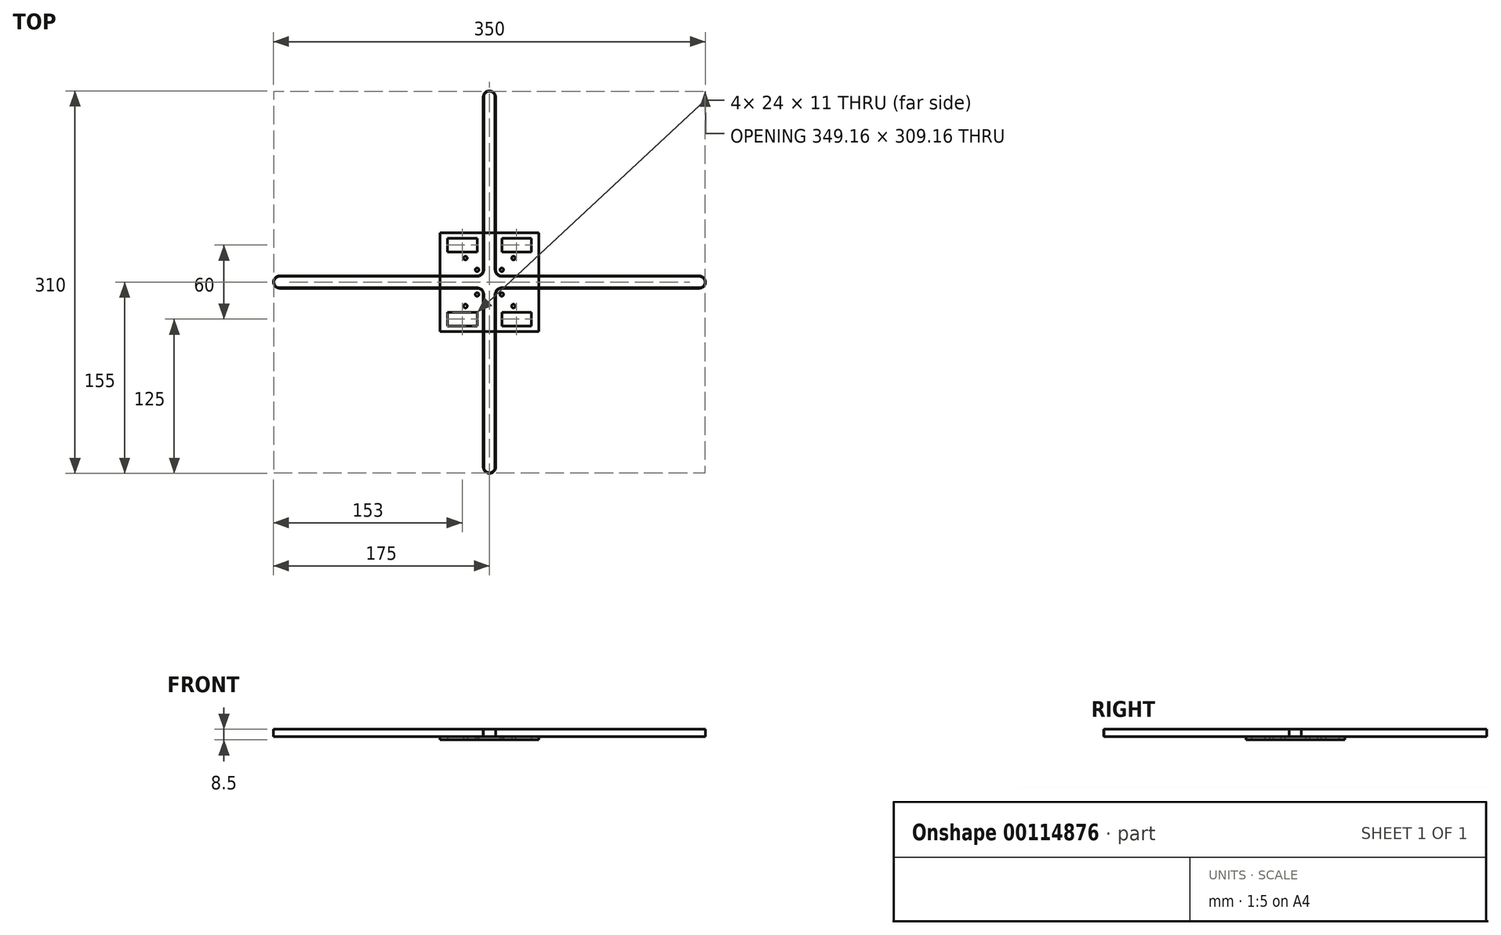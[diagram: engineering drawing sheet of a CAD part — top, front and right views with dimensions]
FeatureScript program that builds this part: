
annotation { "Feature Type Name" : "Feature", "Feature Type Description" : "" }
export const myFeature = defineFeature(function(context is Context, id is Id, definition is map)
    precondition{}
    {
        {
            var Q0;
            Q0=qCreatedBy(makeId("Top.planeOp"),FACE);
            var sketch = newSketch(context, id + "F0", { "sketchPlane" : qUnion([Q0])});
            skLineSegment(sketch, "E0", {"start": v(-126.92, 30) * mm, "end": v(134.24, 30) * mm, "construction": true});
            skLineSegment(sketch, "E1", {"start": v(-126.68, -30) * mm, "end": v(132.4, -30) * mm, "construction": true});
            skLineSegment(sketch, "E2", {"start": v(-22, 80.91) * mm, "end": v(-22, -74.2) * mm, "construction": true});
            skLineSegment(sketch, "E3", {"start": v(22, 83.6) * mm, "end": v(22, -72.05) * mm, "construction": true});
            skLineSegment(sketch, "E4.bottom", {"start": v(-40, 40) * mm, "end": v(40, 40) * mm});
            skLineSegment(sketch, "E4.top", {"start": v(-40, -40) * mm, "end": v(40, -40) * mm});
            skLineSegment(sketch, "E4.left", {"start": v(-40, 40) * mm, "end": v(-40, -40) * mm});
            skLineSegment(sketch, "E4.right", {"start": v(40, 40) * mm, "end": v(40, -40) * mm});
            skPoint(sketch, "E4.middle", {"position": v(0, 0) * mm});
            skLineSegment(sketch, "E5.bottom", {"start": v(-34, 35.5) * mm, "end": v(-10, 35.5) * mm});
            skLineSegment(sketch, "E5.top", {"start": v(-34, 24.5) * mm, "end": v(-10, 24.5) * mm});
            skLineSegment(sketch, "E5.left", {"start": v(-34, 35.5) * mm, "end": v(-34, 24.5) * mm});
            skLineSegment(sketch, "E5.right", {"start": v(-10, 35.5) * mm, "end": v(-10, 24.5) * mm});
            skPoint(sketch, "E5.middle", {"position": v(-22, 30) * mm});
            skLineSegment(sketch, "E6.bottom", {"start": v(10, 35.5) * mm, "end": v(34, 35.5) * mm});
            skLineSegment(sketch, "E6.top", {"start": v(10, 24.5) * mm, "end": v(34, 24.5) * mm});
            skLineSegment(sketch, "E6.left", {"start": v(10, 35.5) * mm, "end": v(10, 24.5) * mm});
            skLineSegment(sketch, "E6.right", {"start": v(34, 35.5) * mm, "end": v(34, 24.5) * mm});
            skPoint(sketch, "E6.middle", {"position": v(22, 30) * mm});
            skLineSegment(sketch, "E7.bottom", {"start": v(-34, -24.5) * mm, "end": v(-10, -24.5) * mm});
            skLineSegment(sketch, "E7.top", {"start": v(-34, -35.5) * mm, "end": v(-10, -35.5) * mm});
            skLineSegment(sketch, "E7.left", {"start": v(-34, -24.5) * mm, "end": v(-34, -35.5) * mm});
            skLineSegment(sketch, "E7.right", {"start": v(-10, -24.5) * mm, "end": v(-10, -35.5) * mm});
            skPoint(sketch, "E7.middle", {"position": v(-22, -30) * mm});
            skLineSegment(sketch, "E8.bottom", {"start": v(10, -24.5) * mm, "end": v(34, -24.5) * mm});
            skLineSegment(sketch, "E8.top", {"start": v(10, -35.5) * mm, "end": v(34, -35.5) * mm});
            skLineSegment(sketch, "E8.left", {"start": v(10, -24.5) * mm, "end": v(10, -35.5) * mm});
            skLineSegment(sketch, "E8.right", {"start": v(34, -24.5) * mm, "end": v(34, -35.5) * mm});
            skPoint(sketch, "E8.middle", {"position": v(22, -30) * mm});
            skLineSegment(sketch, "E9.bottom", {"start": v(-10, 10) * mm, "end": v(10, 10) * mm, "construction": true});
            skLineSegment(sketch, "E9.top", {"start": v(-10, -10) * mm, "end": v(10, -10) * mm, "construction": true});
            skLineSegment(sketch, "E9.left", {"start": v(-10, 10) * mm, "end": v(-10, -10) * mm, "construction": true});
            skLineSegment(sketch, "E9.right", {"start": v(10, 10) * mm, "end": v(10, -10) * mm, "construction": true});
            skCircle(sketch, "E10", {"center": v(-10, 10) * mm, "radius": 1.5 * mm});
            skCircle(sketch, "E11", {"center": v(10, 10) * mm, "radius": 1.5 * mm});
            skCircle(sketch, "E12", {"center": v(-10, -10) * mm, "radius": 1.5 * mm});
            skCircle(sketch, "E13", {"center": v(10, -10) * mm, "radius": 1.5 * mm});
            skCircle(sketch, "E14", {"center": v(-10, 10) * mm, "radius": 5.75 * mm, "construction": true});
            skLineSegment(sketch, "E15", {"start": v(40, 40) * mm, "end": v(-40, -40) * mm, "construction": true});
            skLineSegment(sketch, "E16", {"start": v(-40, 40) * mm, "end": v(40, -40) * mm, "construction": true});
            skCircle(sketch, "E17", {"center": v(0, 0) * mm, "radius": 27.5 * mm, "construction": true});
            skCircle(sketch, "E18", {"center": v(19.44, 19.44) * mm, "radius": 1.5 * mm});
            skCircle(sketch, "E19", {"center": v(-19.44, 19.44) * mm, "radius": 1.5 * mm});
            skCircle(sketch, "E20", {"center": v(-19.44, -19.44) * mm, "radius": 1.5 * mm});
            skCircle(sketch, "E21", {"center": v(19.44, -19.44) * mm, "radius": 1.5 * mm});
            skSolve(sketch);
        }
        {
            var Q0;
            Q0 = qSketchRegion(id + "F0", true);
            extrude(context, id + "F1", {"entities" : qUnion([Q0]), "depth" : 2.5 * mm});
        }
        {
            var Q0;
            Q0=makeQuery(id+"F1.opExtrude","CAP_FACE",FACE,{"disambiguationData":[OSD([sQuery(id+"F0.wireOp",EDGE,"E4.bottom"),sQuery(id+"F0.wireOp",EDGE,"E4.top"),sQuery(id+"F0.wireOp",EDGE,"E4.left"),sQuery(id+"F0.wireOp",EDGE,"E4.right"),sQuery(id+"F0.wireOp",EDGE,"E5.bottom"),sQuery(id+"F0.wireOp",EDGE,"E5.top"),sQuery(id+"F0.wireOp",EDGE,"E5.left"),sQuery(id+"F0.wireOp",EDGE,"E5.right"),sQuery(id+"F0.wireOp",EDGE,"E6.bottom"),sQuery(id+"F0.wireOp",EDGE,"E6.top"),sQuery(id+"F0.wireOp",EDGE,"E6.left"),sQuery(id+"F0.wireOp",EDGE,"E6.right"),sQuery(id+"F0.wireOp",EDGE,"E7.bottom"),sQuery(id+"F0.wireOp",EDGE,"E7.top"),sQuery(id+"F0.wireOp",EDGE,"E7.left"),sQuery(id+"F0.wireOp",EDGE,"E7.right"),sQuery(id+"F0.wireOp",EDGE,"E8.bottom"),sQuery(id+"F0.wireOp",EDGE,"E8.top"),sQuery(id+"F0.wireOp",EDGE,"E8.left"),sQuery(id+"F0.wireOp",EDGE,"E8.right"),sQuery(id+"F0.wireOp",EDGE,"E10"),sQuery(id+"F0.wireOp",EDGE,"E11"),sQuery(id+"F0.wireOp",EDGE,"E12"),sQuery(id+"F0.wireOp",EDGE,"E13")])],"isStart":false});
            var sketch = newSketch(context, id + "F2", { "sketchPlane" : qUnion([Q0])});
            skLineSegment(sketch, "E22", {"start": v(-199.3, 0) * mm, "end": v(227.96, 0) * mm, "construction": true});
            skLineSegment(sketch, "E23", {"start": v(0, 183.41) * mm, "end": v(0, -159.24) * mm, "construction": true});
            skArc(sketch, "E24", {"start": v(-170, 5) * mm, "mid": v(-175, 0) * mm, "end": v(-170, -5) * mm});
            skArc(sketch, "E25", {"start": v(170, -5) * mm, "mid": v(175, 0) * mm, "end": v(170, 5) * mm});
            skArc(sketch, "E26", {"start": v(5, 150) * mm, "mid": v(0, 155) * mm, "end": v(-5, 150) * mm});
            skArc(sketch, "E27", {"start": v(-5, -150) * mm, "mid": v(0, -155) * mm, "end": v(5, -150) * mm});
            skLineSegment(sketch, "E28", {"start": v(-170, 5) * mm, "end": v(-10, 5) * mm});
            skLineSegment(sketch, "E29", {"start": v(-170, -5) * mm, "end": v(-10, -5) * mm});
            skLineSegment(sketch, "E30", {"start": v(10, 5) * mm, "end": v(170, 5) * mm});
            skLineSegment(sketch, "E31", {"start": v(10, -5) * mm, "end": v(170, -5) * mm});
            skLineSegment(sketch, "E32", {"start": v(-5, 150) * mm, "end": v(-5, 10) * mm});
            skLineSegment(sketch, "E33", {"start": v(5, 150) * mm, "end": v(5, 10) * mm});
            skLineSegment(sketch, "E34", {"start": v(-5, -150) * mm, "end": v(-5, -10) * mm});
            skLineSegment(sketch, "E35", {"start": v(5, -150) * mm, "end": v(5, -10) * mm});
            skArc(sketch, "E36", {"start": v(-5, 10) * mm, "mid": v(-6.46, 6.46) * mm, "end": v(-10, 5) * mm});
            skArc(sketch, "E37", {"start": v(10, 5) * mm, "mid": v(6.46, 6.46) * mm, "end": v(5, 10) * mm});
            skArc(sketch, "E38", {"start": v(5, -10) * mm, "mid": v(6.46, -6.46) * mm, "end": v(10, -5) * mm});
            skArc(sketch, "E39", {"start": v(-10, -5) * mm, "mid": v(-6.46, -6.46) * mm, "end": v(-5, -10) * mm});
            skArc(sketch, "E40.0", {"start": v(-170, 4.58) * mm, "mid": v(-174.58, 0) * mm, "end": v(-170, -4.58) * mm});
            skLineSegment(sketch, "E40.1", {"start": v(-170, 4.58) * mm, "end": v(-10, 4.58) * mm});
            skArc(sketch, "E40.2", {"start": v(-4.58, 10) * mm, "mid": v(-6.17, 6.17) * mm, "end": v(-10, 4.58) * mm});
            skLineSegment(sketch, "E40.3", {"start": v(-4.58, 150) * mm, "end": v(-4.58, 10) * mm});
            skArc(sketch, "E40.4", {"start": v(4.58, 150) * mm, "mid": v(0, 154.58) * mm, "end": v(-4.58, 150) * mm});
            skLineSegment(sketch, "E40.5", {"start": v(4.58, -150) * mm, "end": v(4.58, -10) * mm});
            skArc(sketch, "E40.6", {"start": v(-4.58, -150) * mm, "mid": v(0, -154.58) * mm, "end": v(4.58, -150) * mm});
            skLineSegment(sketch, "E40.7", {"start": v(-4.58, -150) * mm, "end": v(-4.58, -10) * mm});
            skArc(sketch, "E40.8", {"start": v(-10, -4.58) * mm, "mid": v(-6.17, -6.17) * mm, "end": v(-4.58, -10) * mm});
            skArc(sketch, "E40.9", {"start": v(4.58, -10) * mm, "mid": v(6.17, -6.17) * mm, "end": v(10, -4.58) * mm});
            skLineSegment(sketch, "E40.10", {"start": v(10, -4.58) * mm, "end": v(170, -4.58) * mm});
            skArc(sketch, "E40.11", {"start": v(170, -4.58) * mm, "mid": v(174.58, 0) * mm, "end": v(170, 4.58) * mm});
            skLineSegment(sketch, "E40.12", {"start": v(10, 4.58) * mm, "end": v(170, 4.58) * mm});
            skArc(sketch, "E40.13", {"start": v(10, 4.58) * mm, "mid": v(6.17, 6.17) * mm, "end": v(4.58, 10) * mm});
            skLineSegment(sketch, "E40.14", {"start": v(-170, -4.58) * mm, "end": v(-10, -4.58) * mm});
            skLineSegment(sketch, "E40.15", {"start": v(4.58, 150) * mm, "end": v(4.58, 10) * mm});
            skSolve(sketch);
        }
        {
            var Q0;
            Q0 = qSketchRegion(id + "F2", true);
            extrude(context, id + "F3", {"entities" : qUnion([Q0]), "depth" : 6 * mm});
        }
    });
